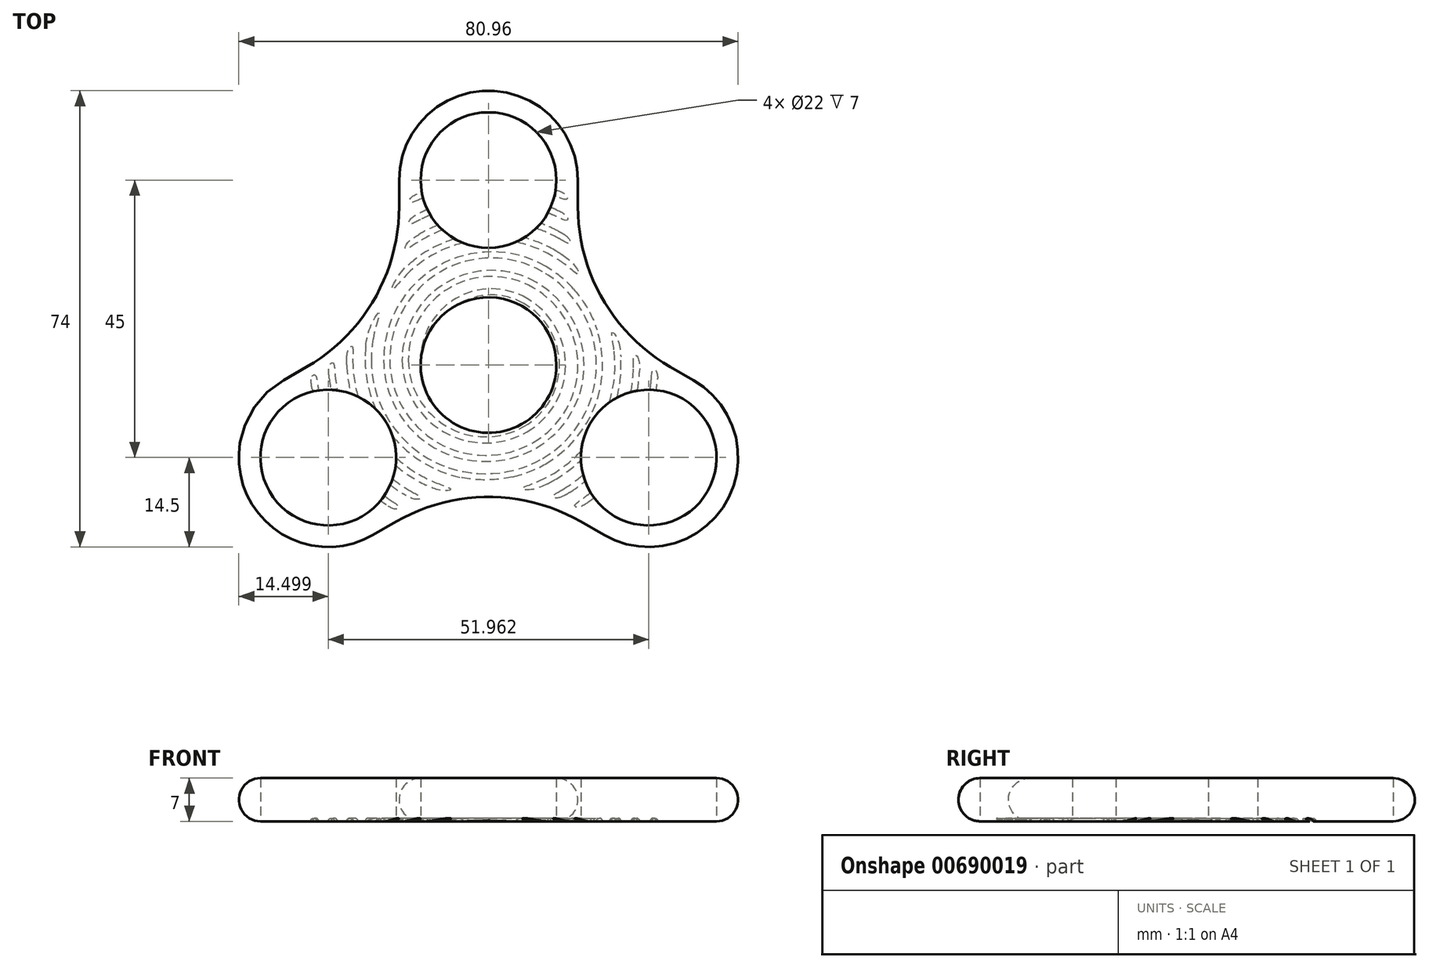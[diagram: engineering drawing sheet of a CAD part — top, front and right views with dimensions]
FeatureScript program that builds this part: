
annotation { "Feature Type Name" : "Feature", "Feature Type Description" : "" }
export const myFeature = defineFeature(function(context is Context, id is Id, definition is map)
    precondition{}
    {
        {
            var Q0;
            Q0=qCreatedBy(makeId("Top.planeOp"),FACE);
            var sketch = newSketch(context, id + "F0", { "sketchPlane" : qUnion([Q0])});
            skCircle(sketch, "E0", {"center": v(0, 0) * mm, "radius": 11 * mm});
            skCircle(sketch, "E1.0", {"center": v(0, 0) * mm, "radius": 14.5 * mm});
            skCircle(sketch, "E2", {"center": v(0, 30) * mm, "radius": 11 * mm});
            skCircle(sketch, "E3.0", {"center": v(0, 30) * mm, "radius": 14.5 * mm});
            skLineSegment(sketch, "E4", {"start": v(-14.5, 30) * mm, "end": v(-14.5, 0) * mm});
            skLineSegment(sketch, "E5", {"start": v(14.5, 30) * mm, "end": v(14.5, 0) * mm});
            skSolve(sketch);
        }
        {
            var Q0;
            Q0 = qSketchRegion(id + "F0", true);
            extrude(context, id + "F1", {"entities" : qUnion([Q0]), "endBound" : BoundingType.SYMMETRIC, "depth" : 7 * mm, "offsetDistance" : 25 * mm});
        }
        {
            var Q0;
            Q0=makeQuery(id+"F1.opExtrude","SWEPT_BODY",BODY,{"disambiguationData":[OSD([sQuery(id+"F0.wireOp",EDGE,"E0"),sQuery(id+"F0.wireOp",EDGE,"E1.0"),sQuery(id+"F0.wireOp",EDGE,"E2"),sQuery(id+"F0.wireOp",EDGE,"E3.0"),sQuery(id+"F0.wireOp",EDGE,"E4"),sQuery(id+"F0.wireOp",EDGE,"E5")])]});
            var Q1;
            Q1=makeQuery(id+"F1.opExtrude","SWEPT_FACE",FACE,{"disambiguationData":[OSD([sQuery(id+"F0.wireOp",EDGE,"E1.0")])]});
            circularPattern(context, id + "F2", {"operationType" : NewBodyOperationType.ADD, "entities" : qUnion([Q0]), "axis" : qUnion([Q1]), "angle" : 360 * degree, "instanceCount" : 3, "equalSpace" : true});
        }
        {
            var Q0;
            Q0=makeQuery(id+"F2.boolean.opBoolean","INTERSECT",EDGE,{"derivedFrom":[makeQuery(id+"F1.opExtrude","SWEPT_FACE",FACE,{"disambiguationData":[OSD([sQuery(id+"F0.wireOp",EDGE,"E4")])]}),makeQuery(id+"F2.opPattern","COPY",FACE,{"derivedFrom":makeQuery(id+"F1.opExtrude","SWEPT_FACE",FACE,{"disambiguationData":[OSD([sQuery(id+"F0.wireOp",EDGE,"E5")])]}),"instanceName":"2"})]});
            var Q1;
            Q1=makeQuery(id+"F2.boolean.opBoolean","INTERSECT",EDGE,{"derivedFrom":[makeQuery(id+"F1.opExtrude","SWEPT_FACE",FACE,{"disambiguationData":[OSD([sQuery(id+"F0.wireOp",EDGE,"E5")])]}),makeQuery(id+"F2.opPattern","COPY",FACE,{"derivedFrom":makeQuery(id+"F1.opExtrude","SWEPT_FACE",FACE,{"disambiguationData":[OSD([sQuery(id+"F0.wireOp",EDGE,"E4")])]}),"instanceName":"1"})]});
            var Q2;
            Q2=makeQuery(id+"F2.boolean.opBoolean","INTERSECT",EDGE,{"derivedFrom":[makeQuery(id+"F2.opPattern","COPY",FACE,{"derivedFrom":makeQuery(id+"F1.opExtrude","SWEPT_FACE",FACE,{"disambiguationData":[OSD([sQuery(id+"F0.wireOp",EDGE,"E5")])]}),"instanceName":"1"}),makeQuery(id+"F2.opPattern","COPY",FACE,{"derivedFrom":makeQuery(id+"F1.opExtrude","SWEPT_FACE",FACE,{"disambiguationData":[OSD([sQuery(id+"F0.wireOp",EDGE,"E4")])]}),"instanceName":"2"})]});
            fillet(context, id + "F3", {"entities" : qUnion([Q0, Q1, Q2]), "radius" : 30 * mm, "tangentPropagation" : true, "defaultsChanged" : false, "vertexSettings" : [], "allowEdgeOverflow" : false});
        }
        {
            var Q0;
            Q0=makeQuery(id+"F1.opExtrude","CAP_EDGE",EDGE,{"disambiguationData":[OSD([sQuery(id+"F0.wireOp",EDGE,"E3.0")])],"isStart":false});
            var Q1;
            Q1=makeQuery(id+"F1.opExtrude","CAP_EDGE",EDGE,{"disambiguationData":[OSD([sQuery(id+"F0.wireOp",EDGE,"E3.0")])],"isStart":true});
            fillet(context, id + "F4", {"entities" : qUnion([Q0, Q1]), "radius" : 3.5 * mm, "tangentPropagation" : true, "allowEdgeOverflow" : false});
        }
        {
            var Q0;
            {var subQ0=makeQuery(id+"F1.opExtrude","CAP_FACE",FACE,{"disambiguationData":[OSD([sQuery(id+"F0.wireOp",EDGE,"E0"),sQuery(id+"F0.wireOp",EDGE,"E1.0"),sQuery(id+"F0.wireOp",EDGE,"E2"),sQuery(id+"F0.wireOp",EDGE,"E3.0"),sQuery(id+"F0.wireOp",EDGE,"E4"),sQuery(id+"F0.wireOp",EDGE,"E5")])],"isStart":true});Q0=makeQuery(id+"F2.boolean.opBoolean","MERGE",FACE,{"derivedFrom":[subQ0,makeQuery(id+"F2.opPattern","COPY",FACE,{"derivedFrom":subQ0,"instanceName":"1"}),makeQuery(id+"F2.opPattern","COPY",FACE,{"derivedFrom":subQ0,"instanceName":"2"})]});}
            var sketch = newSketch(context, id + "F5", { "sketchPlane" : qUnion([Q0])});
            skLineSegment(sketch, "E6", {"start": v(0, 0) * mm, "end": v(-0.5, -0.87) * mm, "construction": true});
            skLineSegment(sketch, "E7", {"start": v(-0.5, -0.87) * mm, "end": v(0.5, -0.87) * mm, "construction": true});
            skLineSegment(sketch, "E8", {"start": v(0.5, -0.87) * mm, "end": v(0, 0) * mm, "construction": true});
            skLineSegment(sketch, "E9", {"start": v(0.5, -0.87) * mm, "end": v(25, -43.3) * mm, "construction": true});
            skLineSegment(sketch, "E10", {"start": v(-0.5, -0.87) * mm, "end": v(-49.5, -0.87) * mm, "construction": true});
            skLineSegment(sketch, "E11", {"start": v(0, 0) * mm, "end": v(24.5, 42.44) * mm, "construction": true});
            skArc(sketch, "E12", {"start": v(0, 0) * mm, "mid": v(-1, 0) * mm, "end": v(-1.5, -0.87) * mm});
            skArc(sketch, "E13", {"start": v(-1.5, -0.87) * mm, "mid": v(-0.5, -2.6) * mm, "end": v(1.5, -2.6) * mm});
            skArc(sketch, "E14", {"start": v(1.5, -2.6) * mm, "mid": v(3, 0) * mm, "end": v(1.5, 2.6) * mm});
            skArc(sketch, "E15", {"start": v(1.5, 2.6) * mm, "mid": v(-2.5, 2.6) * mm, "end": v(-4.5, -0.87) * mm});
            skArc(sketch, "E16", {"start": v(-4.5, -0.87) * mm, "mid": v(-2, -5.2) * mm, "end": v(3, -5.2) * mm});
            skArc(sketch, "E17", {"start": v(3, -5.2) * mm, "mid": v(6, 0) * mm, "end": v(3, 5.2) * mm});
            skArc(sketch, "E18", {"start": v(3, 5.2) * mm, "mid": v(-4, 5.2) * mm, "end": v(-7.5, -0.87) * mm});
            skArc(sketch, "E19", {"start": v(-7.5, -0.87) * mm, "mid": v(-3.5, -7.8) * mm, "end": v(4.5, -7.8) * mm});
            skArc(sketch, "E20", {"start": v(4.5, -7.8) * mm, "mid": v(9, 0) * mm, "end": v(4.5, 7.8) * mm});
            skArc(sketch, "E21", {"start": v(4.5, 7.8) * mm, "mid": v(-5.5, 7.8) * mm, "end": v(-10.5, -0.87) * mm});
            skArc(sketch, "E22", {"start": v(-10.5, -0.87) * mm, "mid": v(-5, -10.4) * mm, "end": v(6, -10.4) * mm});
            skArc(sketch, "E23", {"start": v(6, -10.4) * mm, "mid": v(12, 0) * mm, "end": v(6, 10.4) * mm});
            skArc(sketch, "E24", {"start": v(6, 10.4) * mm, "mid": v(-7, 10.4) * mm, "end": v(-13.5, -0.87) * mm});
            skArc(sketch, "E25", {"start": v(-13.5, -0.87) * mm, "mid": v(-6.5, -13) * mm, "end": v(7.5, -13) * mm});
            skArc(sketch, "E26", {"start": v(7.5, -13) * mm, "mid": v(15, 0) * mm, "end": v(7.5, 13) * mm});
            skArc(sketch, "E27", {"start": v(7.5, 13) * mm, "mid": v(-8.5, 13) * mm, "end": v(-16.5, -0.87) * mm});
            skArc(sketch, "E28", {"start": v(-16.5, -0.87) * mm, "mid": v(-8, -15.59) * mm, "end": v(9, -15.59) * mm});
            skArc(sketch, "E29", {"start": v(9, -15.59) * mm, "mid": v(18, 0) * mm, "end": v(9, 15.59) * mm});
            skArc(sketch, "E30", {"start": v(9, 15.59) * mm, "mid": v(-10, 15.59) * mm, "end": v(-19.5, -0.87) * mm});
            skArc(sketch, "E31", {"start": v(-19.5, -0.87) * mm, "mid": v(-9.5, -18.19) * mm, "end": v(10.5, -18.19) * mm});
            skArc(sketch, "E32", {"start": v(10.5, -18.19) * mm, "mid": v(21, 0) * mm, "end": v(10.5, 18.19) * mm});
            skArc(sketch, "E33", {"start": v(10.5, 18.19) * mm, "mid": v(-11.5, 18.19) * mm, "end": v(-22.5, -0.87) * mm});
            skArc(sketch, "E34", {"start": v(-22.5, -0.87) * mm, "mid": v(-11, -20.78) * mm, "end": v(12, -20.78) * mm});
            skArc(sketch, "E35", {"start": v(12, -20.78) * mm, "mid": v(24, 0) * mm, "end": v(12, 20.78) * mm});
            skArc(sketch, "E36", {"start": v(12, 20.78) * mm, "mid": v(-13, 20.78) * mm, "end": v(-25.5, -0.87) * mm});
            skArc(sketch, "E37", {"start": v(-25.5, -0.87) * mm, "mid": v(-12.5, -23.38) * mm, "end": v(13.5, -23.38) * mm});
            skArc(sketch, "E38", {"start": v(13.5, -23.38) * mm, "mid": v(27, 0) * mm, "end": v(13.5, 23.38) * mm});
            skArc(sketch, "E39", {"start": v(13.5, 23.38) * mm, "mid": v(-14.5, 23.38) * mm, "end": v(-28.5, -0.87) * mm});
            skArc(sketch, "E40", {"start": v(-28.5, -0.87) * mm, "mid": v(-14, -25.98) * mm, "end": v(15, -25.98) * mm});
            skSolve(sketch);
        }
        {
            var Q0;
            Q0=sQuery(id+"F5.wireOp",EDGE,"E11");
            cPlane(context, id + "F6", {"entities" : qUnion([Q0]), "cplaneType" : CPlaneType.LINE_ANGLE, "offset" : 25 * mm, "angle" : 90 * degree, "width" : 150 * mm, "height" : 150 * mm});
        }
        {
            var Q0;
            Q0=qCreatedBy(id+"F6.planeOp",FACE);
            var sketch = newSketch(context, id + "F7", { "sketchPlane" : qUnion([Q0])});
            skCircle(sketch, "E41", {"center": v(0, -3.5) * mm, "radius": 0.5 * mm});
            skSolve(sketch);
        }
        {
            var Q0;
            Q0 = qSketchRegion(id + "F7", true);
            var Q1;
            Q1=sQuery(id+"F5.wireOp",EDGE,"E12");
            var Q2;
            Q2=sQuery(id+"F5.wireOp",EDGE,"E13");
            var Q3;
            Q3=sQuery(id+"F5.wireOp",EDGE,"E14");
            var Q4;
            Q4=sQuery(id+"F5.wireOp",EDGE,"E15");
            var Q5;
            Q5=sQuery(id+"F5.wireOp",EDGE,"E18");
            var Q6;
            Q6=sQuery(id+"F5.wireOp",EDGE,"E19");
            var Q7;
            Q7=sQuery(id+"F5.wireOp",EDGE,"E17");
            var Q8;
            Q8=sQuery(id+"F5.wireOp",EDGE,"E16");
            var Q9;
            Q9=sQuery(id+"F5.wireOp",EDGE,"E39");
            var Q10;
            Q10=sQuery(id+"F5.wireOp",EDGE,"E36");
            var Q11;
            Q11=sQuery(id+"F5.wireOp",EDGE,"E33");
            var Q12;
            Q12=sQuery(id+"F5.wireOp",EDGE,"E30");
            var Q13;
            Q13=sQuery(id+"F5.wireOp",EDGE,"E27");
            var Q14;
            Q14=sQuery(id+"F5.wireOp",EDGE,"E24");
            var Q15;
            Q15=sQuery(id+"F5.wireOp",EDGE,"E21");
            var Q16;
            Q16=sQuery(id+"F5.wireOp",EDGE,"E20");
            var Q17;
            Q17=sQuery(id+"F5.wireOp",EDGE,"E23");
            var Q18;
            Q18=sQuery(id+"F5.wireOp",EDGE,"E26");
            var Q19;
            Q19=sQuery(id+"F5.wireOp",EDGE,"E29");
            var Q20;
            Q20=sQuery(id+"F5.wireOp",EDGE,"E32");
            var Q21;
            Q21=sQuery(id+"F5.wireOp",EDGE,"E35");
            var Q22;
            Q22=sQuery(id+"F5.wireOp",EDGE,"E38");
            var Q23;
            Q23=sQuery(id+"F5.wireOp",EDGE,"E40");
            var Q24;
            Q24=sQuery(id+"F5.wireOp",EDGE,"E37");
            var Q25;
            Q25=sQuery(id+"F5.wireOp",EDGE,"E34");
            var Q26;
            Q26=sQuery(id+"F5.wireOp",EDGE,"E31");
            var Q27;
            Q27=sQuery(id+"F5.wireOp",EDGE,"E28");
            var Q28;
            Q28=sQuery(id+"F5.wireOp",EDGE,"E25");
            var Q29;
            Q29=sQuery(id+"F5.wireOp",EDGE,"E22");
            sweep(context, id + "F8", {"operationType" : NewBodyOperationType.REMOVE, "profiles" : qUnion([Q0]), "path" : qUnion([Q1, Q2, Q3, Q4, Q5, Q6, Q7, Q8, Q9, Q10, Q11, Q12, Q13, Q14, Q15, Q16, Q17, Q18, Q19, Q20, Q21, Q22, Q23, Q24, Q25, Q26, Q27, Q28, Q29])});
        }
    });
